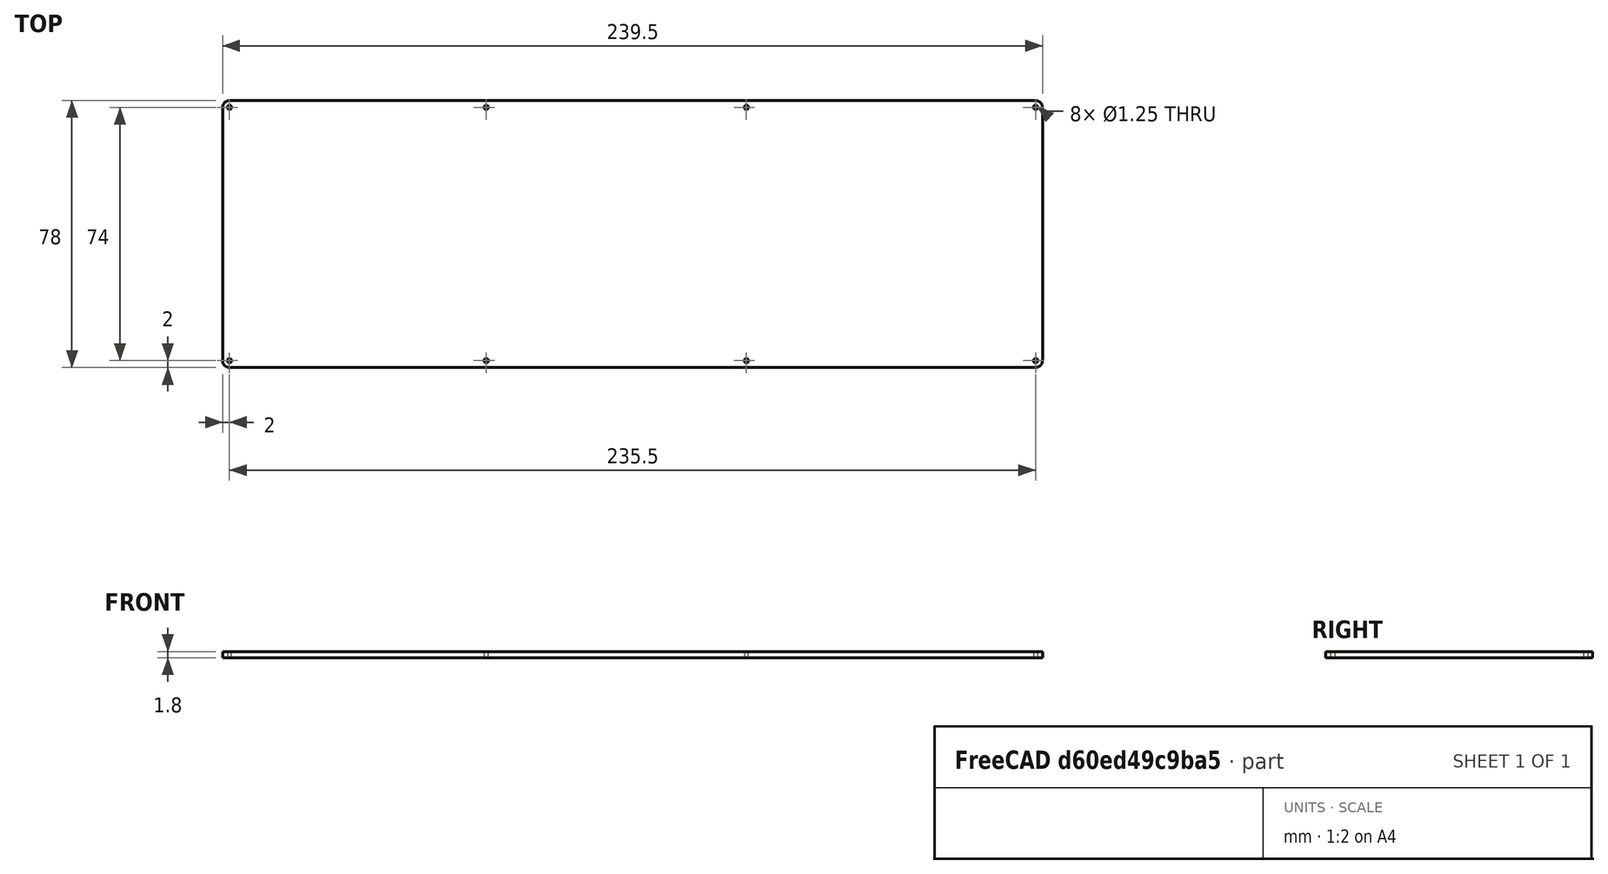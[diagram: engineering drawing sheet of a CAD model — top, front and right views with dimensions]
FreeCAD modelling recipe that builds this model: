
FCSTD DOCUMENT  (FreeCAD 1.0R39285 (Git))
Label: keys-plate
License: All rights reserved
LicenseURL: https://en.wikipedia.org/wiki/All_rights_reserved
objects: Sketcher::SketchObject×1, PartDesign::Pad×1, PartDesign::Body×1
note: 6 computed .brp shape members not serialized (recipe doc carries the construction recipe); baked Part::Feature solids carry a one-line shape summary decoded from their .brp

FEATURE [Sketcher::SketchObject] Sketch
  ArcFitTolerance = 1e-06
  AttachmentSupport = -> [XY_Plane]
  FullyConstrained = true
  MakeInternals = false
  MapMode = 5
  sketch-geometry (20):
    g0: LineSegment StartX=-119.75 StartY=37 StartZ=0 EndX=-119.75 EndY=-37 EndZ=0
    g1: LineSegment StartX=-117.75 StartY=-39 StartZ=0 EndX=117.75 EndY=-39 EndZ=0
    g2: LineSegment StartX=119.75 StartY=-37 StartZ=0 EndX=119.75 EndY=37 EndZ=0
    g3: LineSegment StartX=117.75 StartY=39 StartZ=0 EndX=-117.75 EndY=39 EndZ=0
    g4: ArcOfCircle CenterX=117.75 CenterY=37 CenterZ=0 NormalX=0 NormalY=0 NormalZ=1 AngleXU=0 Radius=2 StartAngle=0 EndAngle=1.5708
    g5: GeomPoint [constr] X=119.75 Y=39 Z=0
    g6: ArcOfCircle CenterX=117.75 CenterY=-37 CenterZ=0 NormalX=0 NormalY=0 NormalZ=1 AngleXU=0 Radius=2 StartAngle=4.71239 EndAngle=6.28319
    g7: GeomPoint [constr] X=119.75 Y=-39 Z=0
    g8: ArcOfCircle CenterX=-117.75 CenterY=-37 CenterZ=0 NormalX=0 NormalY=0 NormalZ=1 AngleXU=0 Radius=2 StartAngle=3.14159 EndAngle=4.71239
    g9: GeomPoint [constr] X=-119.75 Y=-39 Z=0
    g10: ArcOfCircle CenterX=-117.75 CenterY=37 CenterZ=0 NormalX=0 NormalY=0 NormalZ=1 AngleXU=0 Radius=2 StartAngle=1.5708 EndAngle=3.14159
    g11: GeomPoint [constr] X=-119.75 Y=39 Z=0
    g12: Circle CenterX=-117.75 CenterY=37 CenterZ=0 NormalX=0 NormalY=0 NormalZ=1 AngleXU=0 Radius=0.625
    g13: Circle CenterX=117.75 CenterY=37 CenterZ=0 NormalX=0 NormalY=0 NormalZ=1 AngleXU=0 Radius=0.625
    g14: Circle CenterX=117.75 CenterY=-37 CenterZ=0 NormalX=0 NormalY=0 NormalZ=1 AngleXU=0 Radius=0.625
    g15: Circle CenterX=-117.75 CenterY=-37 CenterZ=0 NormalX=0 NormalY=0 NormalZ=1 AngleXU=0 Radius=0.625
    g16: Circle CenterX=33.25 CenterY=-37 CenterZ=0 NormalX=0 NormalY=0 NormalZ=1 AngleXU=0 Radius=0.625
    g17: Circle CenterX=-42.75 CenterY=-37 CenterZ=0 NormalX=0 NormalY=0 NormalZ=1 AngleXU=0 Radius=0.625
    g18: Circle CenterX=33.25 CenterY=37 CenterZ=0 NormalX=0 NormalY=0 NormalZ=1 AngleXU=0 Radius=0.625
    g19: Circle CenterX=-42.75 CenterY=37 CenterZ=0 NormalX=0 NormalY=0 NormalZ=1 AngleXU=0 Radius=0.625
  constraints (47):
    c: Vertical(g0)
    c: Vertical(g2)
    c: Horizontal(g1)
    c: Horizontal(g3)
    c: DistanceY(g9,g11) = 78
    c: DistanceX(g11,g5) = 239.5
    c: Symmetric(g11,g7,g-1)
    c: PointOnObject(g5,g3)
    c: PointOnObject(g5,g2)
    c: Tangent(g3,g4) = -1.5708
    c: Tangent(g2,g4) = -1.5708
    c: PointOnObject(g7,g2)
    c: PointOnObject(g7,g1)
    c: Tangent(g2,g6) = -1.5708
    c: Tangent(g1,g6) = -1.5708
    c: PointOnObject(g9,g1)
    c: PointOnObject(g9,g0)
    c: Tangent(g1,g8) = -1.5708
    c: Tangent(g0,g8) = -1.5708
    c: PointOnObject(g11,g0)
    c: PointOnObject(g11,g3)
    c: Tangent(g0,g10) = -1.5708
    c: Tangent(g3,g10) = -1.5708
    c: Radius(g10) = 2
    c: Equal(g6,g4)
    c: Equal(g4,g8)
    c: Equal(g8,g10)
    c: Diameter(g12) = 1.25
    c: Coincident(g12,g10)
    c: Equal(g12,g15)
    c: Equal(g15,g14)
    c: Equal(g14,g13)
    c: Coincident(g15,g8)
    c: Coincident(g13,g4)
    c: Coincident(g14,g6)
    c: Horizontal(g17,g16)
    c: Horizontal(g16,g8)
    c: Equal(g19,g18)
    c: Equal(g18,g17)
    c: Equal(g17,g16)
    c: Horizontal(g19,g18)
    c: Vertical(g18,g16)
    c: Vertical(g19,g17)
    c: DistanceX(g8,g17) = 75
    c: DistanceX(g17,g16) = 76
    c: Equal(g12,g19)
    c: Horizontal(g10,g19)
FEATURE [PartDesign::Pad] Pad
  Direction = (0,0,1)
  Length = 1.8
  Length2 = 10
  Profile = -> Sketch
  ReferenceAxis = -> Sketch [N_Axis]
  Refine = true
  Suppressed = false
  Type = 0
FEATURE [PartDesign::Body] Body
  AllowCompound = false
  Group = -> [Sketch,Pad]
  Origin = -> Origin
  Tip = -> Pad
